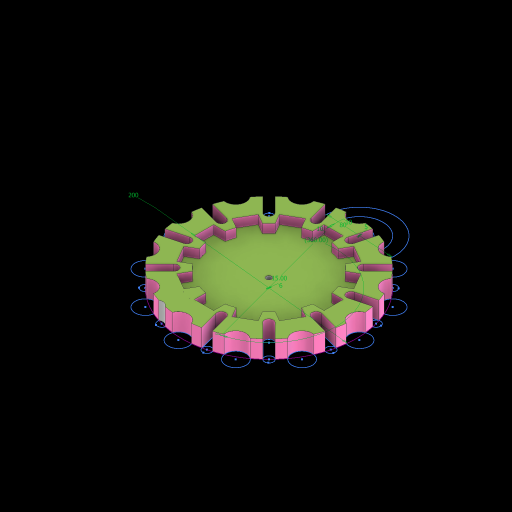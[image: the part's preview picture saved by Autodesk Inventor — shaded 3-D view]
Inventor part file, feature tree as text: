
AUTODESK INVENTOR PART (.ipt)
format: ipt  version: 2023 (Build 270158000, 158)  size: 564,736 bytes
history: native  units: mm
features: sketch x4, extrude x4
ambient origin geometry x8: Origin, YZ Plane, XZ Plane, XY Plane, X Axis, Y Axis, Z Axis, Center Point
bodies: Solid1 (feature_tree)
feature tree (8):
  sketch  "Sketch1"  dims[d1=80.0mm d2=100.0mm d3=22.5deg d4=20.712mm d5=50.0mm d6=54.123064mm d7=10.0mm d8=25.858174mm d9=65.0mm d10=360.0deg d11=7.0mm d12=7.0mm d13=15.0mm d14=15.0mm d15=10.0mm d16=200.0mm]
  sketch  "Sketch2"  dims[d17=15.0deg d19=90.0deg]
  extrude  "Extrusion1"  Depth=10.0mm
  extrude  "Extrusion2"  TaperAngle=90.0deg  [1 undecoded]
  extrude  "Extrusion3"  Depth=10.0mm
  extrude  "Extrusion4"  Depth=20.0mm TaperAngle=360.0deg
  sketch  "Sketch3"  dims[d20=10.0mm d21=10.0mm]
  sketch  "Sketch4"  dims[d22=80.0mm d23=120.0mm d25=360.0deg d27=6.0mm d28=5.0mm d29=20.0mm d30=0.0mm d34=120.0mm d36=360.0deg d38=10.0mm d39=0.0mm d40=20.0mm d41=0.0mm d42=20.0mm d43=0.0mm]
note: 1 required parameter value undecoded (feature->parameter linkage not recoverable at this tier; creation-order binding heuristic only, values carry confidence <= 0.55)
